# Revit family: for update_452909_new
name_source: partatom
category: Plumbing Fixtures
revit_build: Autodesk Revit 2018 (Build: 20170223_1515(x64)
units: mm (PartAtom-declared; Revit-internal decimal feet)

## family parameters
Cut with Voids When Loaded = No
Host = Face
OmniClass Number = 23.31.19.00
OmniClass Title = Toilets
Part Type = Normal
Room Calculation Point = No
Round Connector Dimension = Use Diameter
Shared = No

## types (2) — shared parameters
Always visible = Yes
Connector Description = Water Inlet 55 mm
Default Elevation = 1219 mm
Depth = 570 mm  [stored 1.87008 ft]
Description = Duravit ME by Starck Toilet set wall-mounted 373,5x570x395 mm - 45290900A1 Duravit ME by Starck Toilet set wall-mounted 373,5x570x395 mm - 45290900A11
Diameter = 55  [stored 0.180446 ft]
Edition number = 1
Height = 395 mm  [stored 1.29593 ft]
IFC Classification = Sanitary Terminal
Manufacturer = Duravit
Manufacturer name = DURAVIT AG
Masterformat 2014 Code = 01 52 19
Masterformat 2014 Description = Sanitary Facilities
Material 1 = Duravit - Ceramic - 00 - White Alpin
Material 2 = Duravit - Metal - Chrome
Material main = Ceramics
Model = ME by Starck Toilet set wall-mounted 373,5x570x395 mm - 452909
OmniClass Code = 23-31 19 00
OmniClass Description = Toilets
Outlet Connector Description = Sanitary outlet 102 mm
Outlet Diameter = 102
Product Guid = e566b45e-f38f-4535-9db9-cb8e6494c623
Product SKU = ME-by-Starck-Toilet-set-wall-mounted--3735x570x395-mm-452909
Product data url = https://bimobject.com
Product name = ME by Starck Toilet set wall-mounted  373,5x570x395 mm - 452909
QR code = https://bimobject.com
UNSPSC Code = 301815
URL = http://pro.duravit.com
Uniclass 2015 Code = Pr_40_20_93
Uniclass 2015 Name = Urinal and WC fittings
Uniformat II Code = D2030
Uniformat II Description = Sanitary Waste
Weight = 28.60 kg
Width = 374 mm

## type names (no varying parameters)
- ME by Starck Toilet set wall-mounted 373,5x570x395 mm - 45290900A1
- ME by Starck Toilet set wall-mounted 373,5x570x395 mm - 45290900A11

note: [stored X ft] marks values corroborated as IEEE doubles in the binary element streams (Revit-internal decimal feet)

## geometry (parser evidence)
native form markers: Sweep x6
no freeform markers — native parametric forms only
